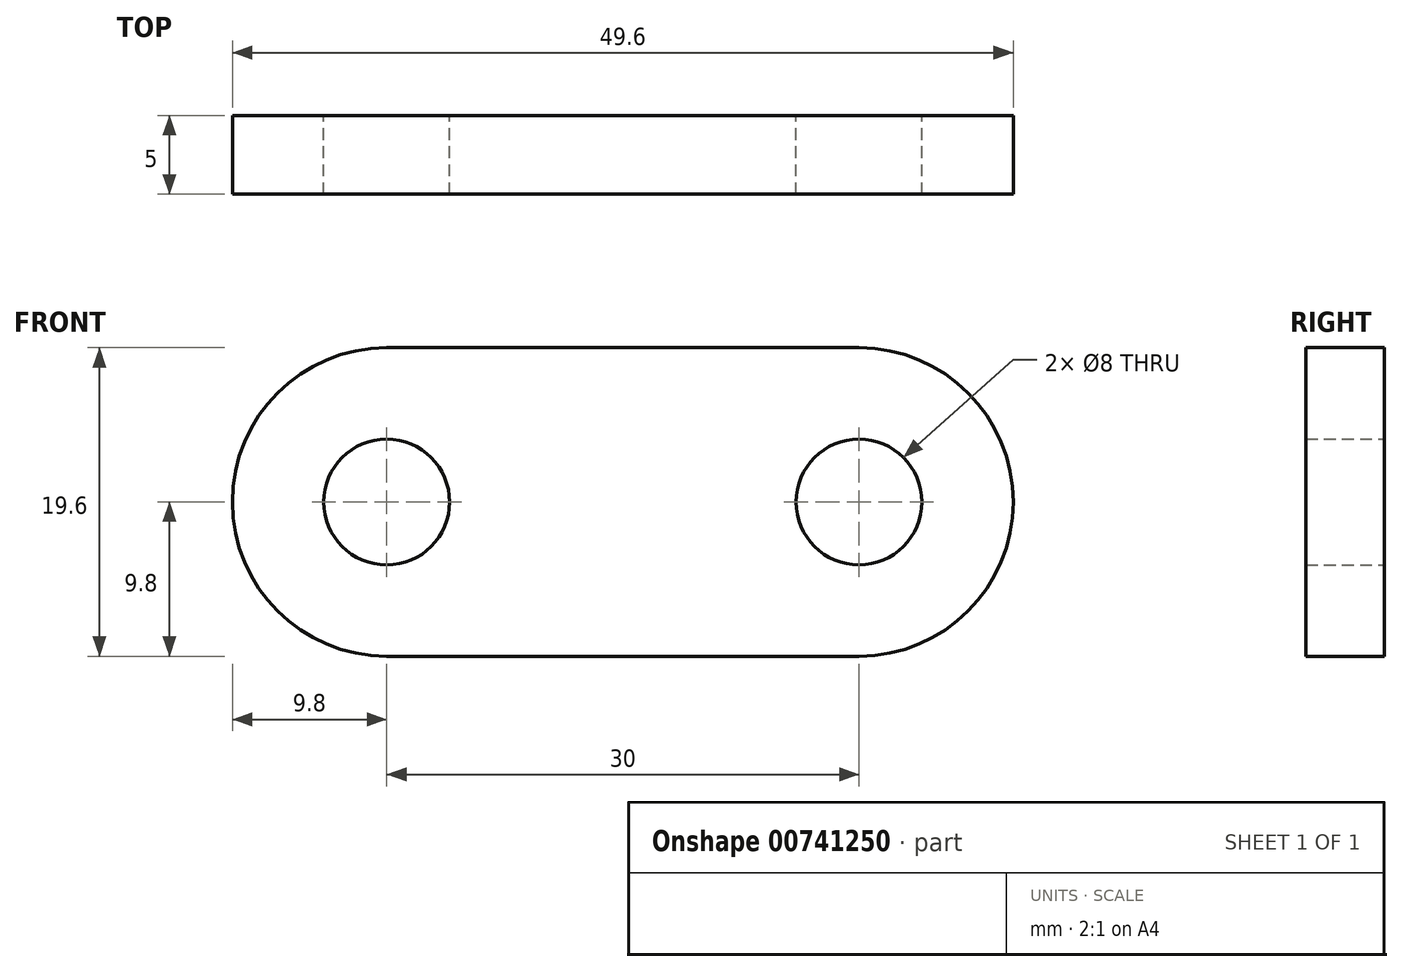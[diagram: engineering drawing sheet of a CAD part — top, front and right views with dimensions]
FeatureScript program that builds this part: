
annotation { "Feature Type Name" : "Feature", "Feature Type Description" : "" }
export const myFeature = defineFeature(function(context is Context, id is Id, definition is map)
    precondition{}
    {
        {
            var Q0;
            Q0=qCreatedBy(makeId("Front.planeOp"),FACE);
            var sketch = newSketch(context, id + "F0", { "sketchPlane" : qUnion([Q0])});
            skLineSegment(sketch, "E0", {"start": v(-27.78, 0) * mm, "end": v(35.32, 0) * mm, "construction": true});
            skLineSegment(sketch, "E1", {"start": v(0, 25.74) * mm, "end": v(0, -29.64) * mm, "construction": true});
            skLineSegment(sketch, "E2", {"start": v(0, 9.8) * mm, "end": v(-15, 9.8) * mm});
            skLineSegment(sketch, "E3.MirrorCS", {"start": v(0, -9.8) * mm, "end": v(-15, -9.8) * mm});
            skArc(sketch, "E4", {"start": v(-15, 9.8) * mm, "mid": v(-24.8, 0) * mm, "end": v(-15, -9.8) * mm});
            skCircle(sketch, "E5", {"center": v(-15, 0) * mm, "radius": 4 * mm});
            skLineSegment(sketch, "E6.MirrorCS", {"start": v(0, 9.8) * mm, "end": v(15, 9.8) * mm});
            skArc(sketch, "E7.MirrorCS", {"start": v(15, 9.8) * mm, "mid": v(24.8, 0) * mm, "end": v(15, -9.8) * mm});
            skCircle(sketch, "E8.MirrorC", {"center": v(15, 0) * mm, "radius": 4 * mm});
            skLineSegment(sketch, "E9.MirrorCS", {"start": v(0, -9.8) * mm, "end": v(15, -9.8) * mm});
            skSolve(sketch);
        }
        {
            var Q0;
            Q0 = qSketchRegion(id + "F0", true);
            extrude(context, id + "F1", {"entities" : qUnion([Q0]), "depth" : 5 * mm, "offsetDistance" : 25.4 * mm});
        }
    });
